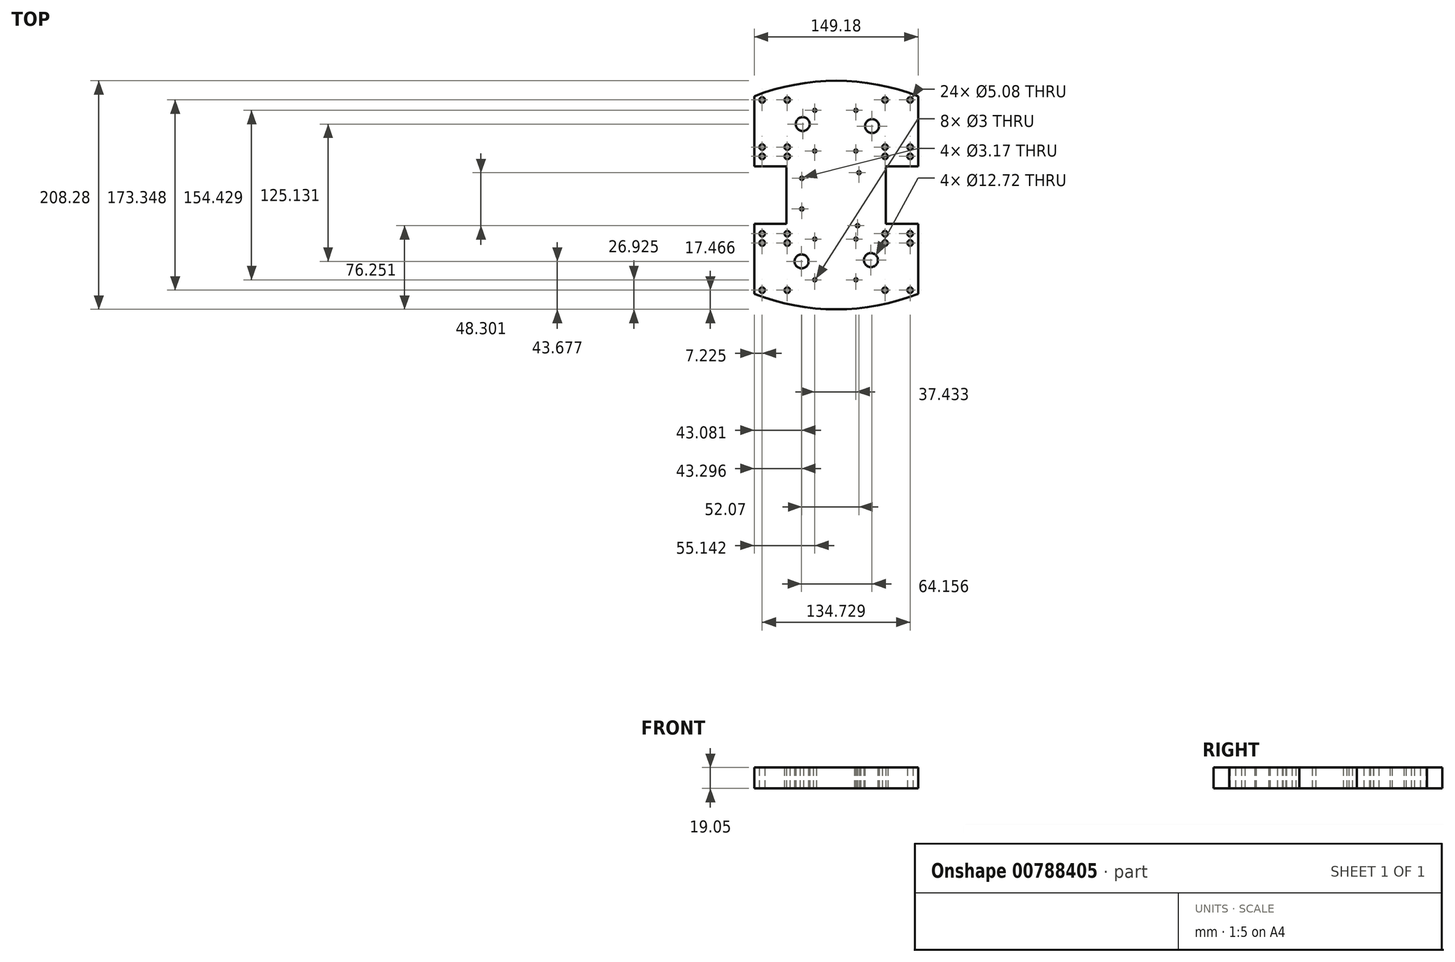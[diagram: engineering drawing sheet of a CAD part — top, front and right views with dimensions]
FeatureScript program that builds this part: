
annotation { "Feature Type Name" : "Feature", "Feature Type Description" : "" }
export const myFeature = defineFeature(function(context is Context, id is Id, definition is map)
    precondition{}
    {
        {
            var Q0;
            Q0=qCreatedBy(makeId("Top.planeOp"),FACE);
            var sketch = newSketch(context, id + "F0", { "sketchPlane" : qUnion([Q0])});
            skLineSegment(sketch, "E0", {"start": v(74.59, 90) * mm, "end": v(74.59, 26.13) * mm});
            skLineSegment(sketch, "E1", {"start": v(74.59, 26.13) * mm, "end": v(45.31, 26.13) * mm});
            skCircle(sketch, "E2", {"center": v(44.5, 86.67) * mm, "radius": 2.54 * mm});
            skCircle(sketch, "E3", {"center": v(67.36, 86.67) * mm, "radius": 2.54 * mm});
            skCircle(sketch, "E4", {"center": v(44.5, 35.22) * mm, "radius": 2.54 * mm});
            skCircle(sketch, "E5", {"center": v(67.36, 35.22) * mm, "radius": 2.54 * mm});
            skCircle(sketch, "E6", {"center": v(44.5, 43.68) * mm, "radius": 2.54 * mm});
            skCircle(sketch, "E7", {"center": v(67.36, 43.68) * mm, "radius": 2.54 * mm});
            skCircle(sketch, "E8.MirrorC", {"center": v(-44.5, 35.22) * mm, "radius": 2.54 * mm});
            skCircle(sketch, "E9.MirrorC", {"center": v(-44.5, 43.68) * mm, "radius": 2.54 * mm});
            skCircle(sketch, "E10.MirrorC", {"center": v(-67.36, 43.68) * mm, "radius": 2.54 * mm});
            skCircle(sketch, "E11.MirrorC", {"center": v(-67.36, 86.67) * mm, "radius": 2.54 * mm});
            skCircle(sketch, "E12.MirrorC", {"center": v(-67.36, 35.22) * mm, "radius": 2.54 * mm});
            skCircle(sketch, "E13.MirrorC", {"center": v(-44.5, 86.67) * mm, "radius": 2.54 * mm});
            skLineSegment(sketch, "E14.MirrorCS", {"start": v(-74.59, 26.13) * mm, "end": v(-45.31, 26.13) * mm});
            skLineSegment(sketch, "E15.MirrorCS", {"start": v(-74.59, 90) * mm, "end": v(-74.59, 26.13) * mm});
            skCircle(sketch, "E16", {"center": v(17.99, 40.13) * mm, "radius": 1.5 * mm});
            skCircle(sketch, "E17", {"center": v(17.99, 77.21) * mm, "radius": 1.5 * mm});
            skCircle(sketch, "E18", {"center": v(-19.45, 77.21) * mm, "radius": 1.5 * mm});
            skCircle(sketch, "E19", {"center": v(-19.45, 40.13) * mm, "radius": 1.5 * mm});
            skCircle(sketch, "E20", {"center": v(20.78, 20.41) * mm, "radius": 1.59 * mm});
            skCircle(sketch, "E21", {"center": v(-31.28, 15.3) * mm, "radius": 1.59 * mm});
            skCircle(sketch, "E22", {"center": v(19.5, -27.89) * mm, "radius": 1.59 * mm});
            skCircle(sketch, "E23", {"center": v(-31.3, -12.66) * mm, "radius": 1.59 * mm});
            skCircle(sketch, "E24.MirrorC", {"center": v(-44.5, -43.68) * mm, "radius": 2.54 * mm});
            skCircle(sketch, "E25.MirrorC", {"center": v(67.36, -86.67) * mm, "radius": 2.54 * mm});
            skCircle(sketch, "E26.MirrorC", {"center": v(67.36, -35.22) * mm, "radius": 2.54 * mm});
            skCircle(sketch, "E27.MirrorC", {"center": v(-67.36, -35.22) * mm, "radius": 2.54 * mm});
            skCircle(sketch, "E28.MirrorC", {"center": v(44.5, -86.67) * mm, "radius": 2.54 * mm});
            skCircle(sketch, "E29.MirrorC", {"center": v(17.99, -77.21) * mm, "radius": 1.5 * mm});
            skCircle(sketch, "E30.MirrorC", {"center": v(44.5, -35.22) * mm, "radius": 2.54 * mm});
            skCircle(sketch, "E31.MirrorC", {"center": v(-19.45, -77.21) * mm, "radius": 1.5 * mm});
            skCircle(sketch, "E32.MirrorC", {"center": v(44.5, -43.68) * mm, "radius": 2.54 * mm});
            skCircle(sketch, "E33.MirrorC", {"center": v(67.36, -43.68) * mm, "radius": 2.54 * mm});
            skCircle(sketch, "E34.MirrorC", {"center": v(17.99, -40.13) * mm, "radius": 1.5 * mm});
            skCircle(sketch, "E35.MirrorC", {"center": v(-44.5, -35.22) * mm, "radius": 2.54 * mm});
            skCircle(sketch, "E36.MirrorC", {"center": v(-44.5, -86.67) * mm, "radius": 2.54 * mm});
            skCircle(sketch, "E37.MirrorC", {"center": v(-19.45, -40.13) * mm, "radius": 1.5 * mm});
            skCircle(sketch, "E38.MirrorC", {"center": v(-67.36, -43.68) * mm, "radius": 2.54 * mm});
            skCircle(sketch, "E39.MirrorC", {"center": v(-67.36, -86.67) * mm, "radius": 2.54 * mm});
            skLineSegment(sketch, "E40.MirrorCS", {"start": v(74.59, -90) * mm, "end": v(74.59, -26.13) * mm});
            skLineSegment(sketch, "E41.MirrorCS", {"start": v(-74.59, -26.13) * mm, "end": v(-45.31, -26.13) * mm});
            skLineSegment(sketch, "E42.MirrorCS", {"start": v(-74.59, -90) * mm, "end": v(-74.59, -26.13) * mm});
            skLineSegment(sketch, "E43.MirrorCS", {"start": v(74.59, -26.13) * mm, "end": v(45.31, -26.13) * mm});
            skLineSegment(sketch, "E44", {"start": v(-45.31, 26.13) * mm, "end": v(-45.31, -26.13) * mm});
            skLineSegment(sketch, "E45", {"start": v(45.31, 26.13) * mm, "end": v(45.31, -26.13) * mm});
            skArc(sketch, "E46", {"start": v(74.59, 90) * mm, "mid": v(0, 104.14) * mm, "end": v(-74.59, 90) * mm});
            skArc(sketch, "E47.MirrorCS", {"start": v(74.59, -90) * mm, "mid": v(0, -104.14) * mm, "end": v(-74.59, -90) * mm});
            skCircle(sketch, "E48", {"center": v(-30.46, 64.67) * mm, "radius": 6.36 * mm});
            skCircle(sketch, "E49", {"center": v(32.65, 62.83) * mm, "radius": 6.36 * mm});
            skCircle(sketch, "E50", {"center": v(-31.5, -60.46) * mm, "radius": 6.36 * mm});
            skCircle(sketch, "E51", {"center": v(31.67, -59.27) * mm, "radius": 6.36 * mm});
            skSolve(sketch);
        }
        {
            var Q0;
            Q0=makeQuery(id+"F0.imprint","IMPRINT",FACE,{"disambiguationData":[TD([[makeQuery(id+"F0.imprint","IMPRINT",EDGE,{"derivedFrom":sQuery(id+"F0.wireOp",EDGE,"E0")}),-1.0]])]});
            extrude(context, id + "F1", {"entities" : qUnion([Q0]), "depth" : 19.05 * mm, "offsetDistance" : 25.4 * mm});
        }
    });
